# Revit family: 306_bdd5c911e7fd4e86ae349a0c16c91d
name_source: partatom
category: Pipe Accessories
units: mm (PartAtom-declared; Revit-internal decimal feet)

## family parameters
Always vertical = Yes
Cut with Voids When Loaded = No
Part Type = Valve - Breaks Into
Round Connector Dimension = Use Diameter
Shared = No
Work Plane-Based = No

## types (1)
- 2105
    A = 60 mm  [stored 0.19685 ft]
    A2 = 25 mm  [stored 0.082021 ft]
    CenSd_L17_6 = 16 mm  [stored 0.0524934 ft]
    CenSd_R3_6 = 12 mm  [stored 0.0393701 ft]
    D = 15 mm
    Default Elevation = 0 mm  [stored 0 ft]
    Description = Autom. filling unit, set pressure, check valve, ½” M-F conn.
    H2HH = 9 mm
    H2HH__ve = -9 mm
    HH = 15 mm  [stored 0.0492126 ft]
    L15 = 1 mm  [stored 0.00328084 ft]
    L16 = 16 mm  [stored 0.0524934 ft]
    L17 = 18 mm  [stored 0.0590551 ft]
    L177 = 17 mm  [stored 0.0557743 ft]
    L177__ve = -17 mm  [stored -0.0557743 ft]
    L2 = 55 mm  [stored 0.180446 ft]
    L22 = 10 mm  [stored 0.0328084 ft]
    L25 = 25 mm  [stored 0.082021 ft]
    L2D = 110 mm
    L2D_Min = 3048 mm  [stored 10 ft]
    L5 = 5 mm  [stored 0.0164042 ft]
    L5__ve = -5 mm  [stored -0.0164042 ft]
    LH = 30 mm  [stored 0.0984252 ft]
    LL = 2 mm  [stored 0.00656168 ft]
    LNT12 = 8 mm  [stored 0.0262467 ft]
    LNT2 = 43 mm
    LNT2__ve = -43 mm
    MC Product Code = 2105
    Manufacturer = FAR
    NT = 12 mm  [stored 0.0393701 ft]
    NT__ve = -12 mm
    QmdConnectorList = 301;D;302;D
    R = 8 mm  [stored 0.0262467 ft]
    R1 = 12 mm  [stored 0.0393701 ft]
    R2 = 10 mm  [stored 0.0328084 ft]
    R21 = 11 mm  [stored 0.0360892 ft]
    R3 = 14 mm  [stored 0.0459318 ft]
    RR = 3 mm  [stored 0.00984252 ft]
    RR1 = 21 mm  [stored 0.0688976 ft]
    RR2 = 26 mm  [stored 0.0853018 ft]
    W2D = 15 mm  [stored 0.0492126 ft]
    magiPartTypeId = 306
    magiProductFamilyId = bdd5c911e7fd4e86ae349a0c16c91d
    magiProductId = 76d3b077d6df4884a027f9f95aa827

note: [stored X ft] marks values corroborated as IEEE doubles in the binary element streams (Revit-internal decimal feet)

## geometry (parser evidence)
native form markers: Sweep x1
no freeform markers — native parametric forms only
